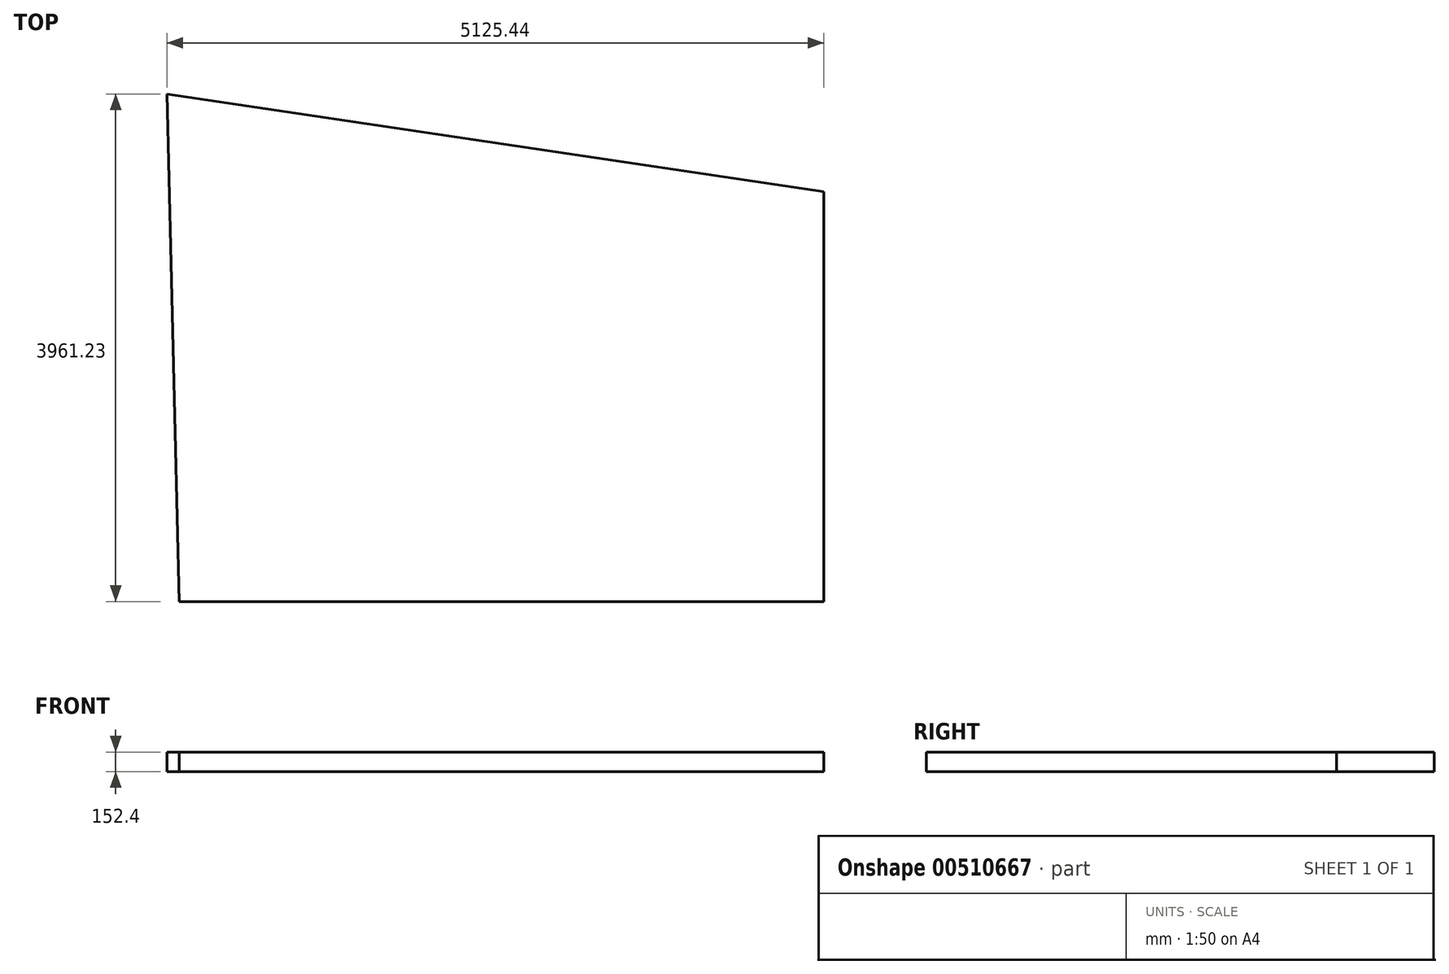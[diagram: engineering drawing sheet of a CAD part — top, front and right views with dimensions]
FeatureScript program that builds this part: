
annotation { "Feature Type Name" : "Feature", "Feature Type Description" : "" }
export const myFeature = defineFeature(function(context is Context, id is Id, definition is map)
    precondition{}
    {
        {
            var Q0;
            Q0=qCreatedBy(makeId("Top.planeOp"),FACE);
            var sketch = newSketch(context, id + "F0", { "sketchPlane" : qUnion([Q0])});
            skLineSegment(sketch, "E0", {"start": v(96.24, -329.78) * mm, "end": v(96.24, -3530.18) * mm});
            skLineSegment(sketch, "E1", {"start": v(96.24, -3530.18) * mm, "end": v(-4932.96, -3530.18) * mm});
            skLineSegment(sketch, "E2", {"start": v(96.24, -329.78) * mm, "end": v(-5029.2, 431.05) * mm});
            skLineSegment(sketch, "E3", {"start": v(-5029.2, 431.05) * mm, "end": v(-4932.96, -3530.18) * mm});
            skSolve(sketch);
        }
        {
            var Q0;
            Q0 = qSketchRegion(id + "F0", true);
            extrude(context, id + "F1", {"entities" : qUnion([Q0]), "depth" : 152.4 * mm, "offsetDistance" : 30.48 * mm});
        }
    });
